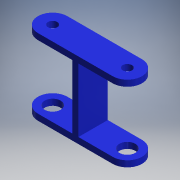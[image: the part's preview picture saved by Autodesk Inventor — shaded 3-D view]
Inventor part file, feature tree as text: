
AUTODESK INVENTOR PART (.ipt)
format: ipt  version: 2017 (Build 210142000, 142)  size: 143,360 bytes
history: native  units: mm (DEFAULTED — no unit token found)
features: extrude x4, sketch x4, fillet x1
ambient origin geometry x8: Origin, YZ Plane, XZ Plane, XY Plane, X Axis, Y Axis, Z Axis, Center Point
bodies: Body1 (feature_tree)
feature tree (9):
  extrude  "Extrusion3"  Depth=24.0mm
  extrude  "Extrusion4"  TaperAngle=0.0deg  [1 undecoded]
  fillet  "Fillet4"  Radius=5.0mm
  extrude  "Extrusion7"  Depth=45.0mm
  extrude  "Extrusion8"  Depth=12.0mm
  sketch  "Sketch3"  dims[d6=5.0mm d7=24.0mm]
  sketch  "Sketch4"  dims[d8=62.0mm d9=0.0mm d10=5.0mm]
  sketch  "Sketch8"  dims[d11=40.0mm d12=0.0mm d24=45.0mm]
  sketch  "Sketch9"  dims[d25=0.0mm d26=12.0mm d27=7.5mm d28=10.0mm d29=0.0mm d30=13.0mm d31=10.0mm d32=0.0mm]
note: 1 required parameter value undecoded (feature->parameter linkage not recoverable at this tier; creation-order binding heuristic only, values carry confidence <= 0.55)
